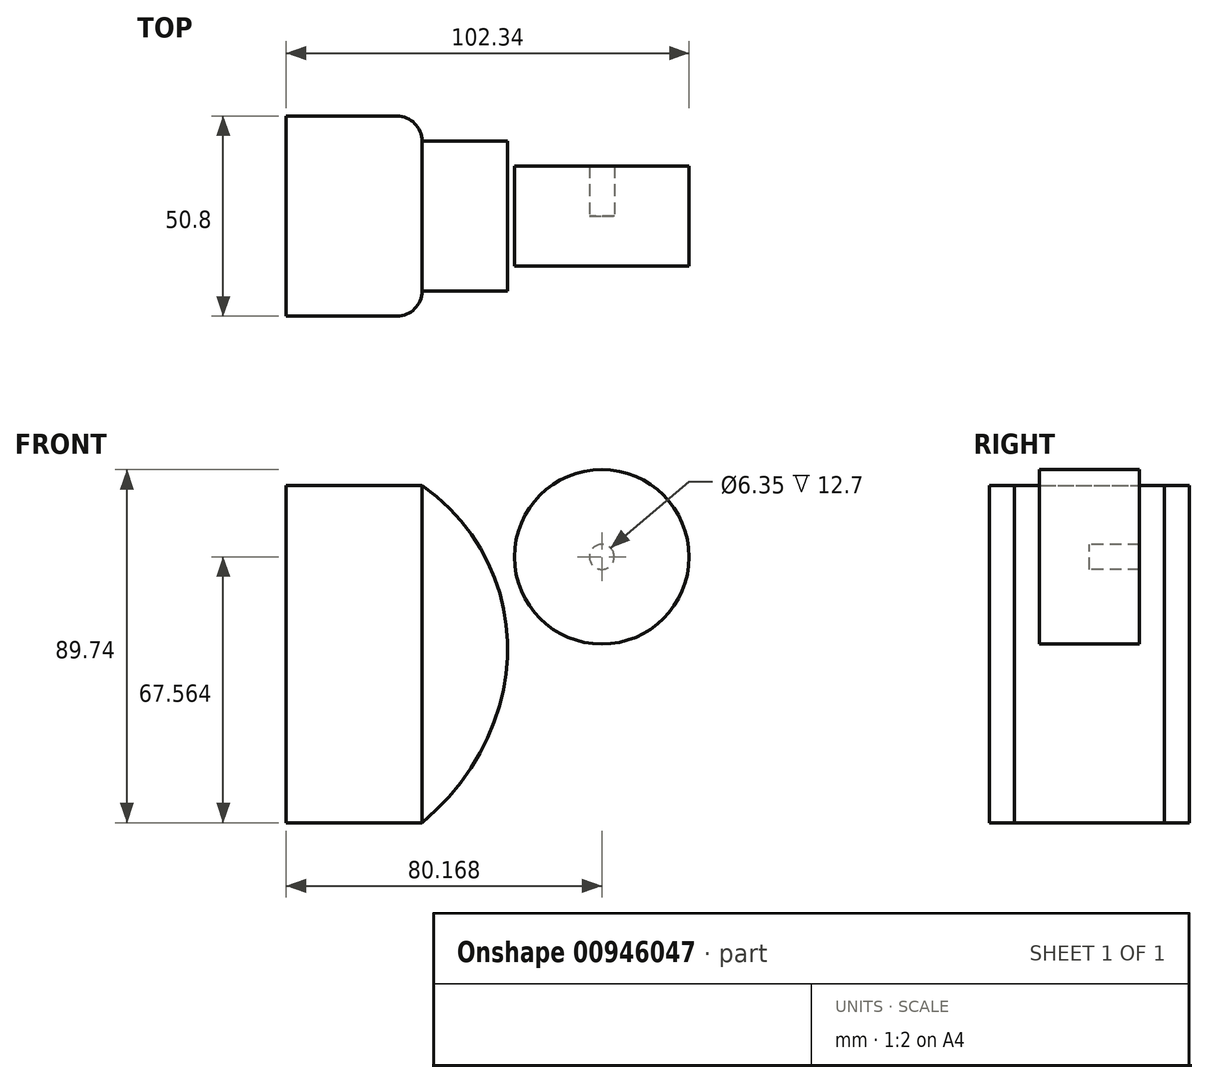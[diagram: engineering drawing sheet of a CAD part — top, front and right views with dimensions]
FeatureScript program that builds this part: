
annotation { "Feature Type Name" : "Feature", "Feature Type Description" : "" }
export const myFeature = defineFeature(function(context is Context, id is Id, definition is map)
    precondition{}
    {
        {
            var Q0;
            Q0=qCreatedBy(makeId("Front.planeOp"),FACE);
            var sketch = newSketch(context, id + "F0", { "sketchPlane" : qUnion([Q0])});
            skLineSegment(sketch, "E0.bottom", {"start": v(-47.09, -46.4) * mm, "end": v(-12.6, -46.4) * mm});
            skLineSegment(sketch, "E0.top", {"start": v(-47.09, 39.32) * mm, "end": v(-12.6, 39.32) * mm});
            skLineSegment(sketch, "E0.left", {"start": v(-47.09, -46.4) * mm, "end": v(-47.09, 39.32) * mm});
            skLineSegment(sketch, "E0.right", {"start": v(-12.6, -46.4) * mm, "end": v(-12.6, 39.32) * mm});
            skFitSpline(sketch, "E1", {"points": [v(-12.6, 39.32) * mm, v(-12.6, -46.4) * mm], "startDerivative": vector(87.62, -62.5) * mm, "endDerivative": vector(-86.21, -72.18) * mm});
            skCircle(sketch, "E2", {"center": v(33.08, 21.16) * mm, "radius": 22.18 * mm});
            skCircle(sketch, "E3.0", {"center": v(33.08, 21.16) * mm, "radius": 9.48 * mm});
            skSolve(sketch);
        }
        {
            var Q0;
            Q0=makeQuery(id+"F0.imprint","IMPRINT",FACE,{"disambiguationData":[TD([[makeQuery(id+"F0.imprint","IMPRINT",EDGE,{"derivedFrom":sQuery(id+"F0.wireOp",EDGE,"E0.bottom")}),1.0]])]});
            extrude(context, id + "F1", {"entities" : qUnion([Q0]), "endBound" : BoundingType.SYMMETRIC, "depth" : 50.8 * mm, "offsetDistance" : 25.4 * mm});
        }
        {
            var Q0;
            Q0=makeQuery(id+"F0.imprint","IMPRINT",FACE,{"disambiguationData":[TD([[makeQuery(id+"F0.imprint","IMPRINT",EDGE,{"derivedFrom":sQuery(id+"F0.wireOp",EDGE,"E0.right")}),-1.0]])]});
            extrude(context, id + "F2", {"entities" : qUnion([Q0]), "operationType" : NewBodyOperationType.ADD, "endBound" : BoundingType.SYMMETRIC, "depth" : 38.1 * mm, "offsetDistance" : 25.4 * mm});
        }
        {
            var Q0;
            Q0=makeQuery(id+"F1.opExtrude","CAP_EDGE",EDGE,{"disambiguationData":[OSD([sQuery(id+"F0.wireOp",EDGE,"E0.right")])],"isStart":false});
            var Q1;
            Q1=makeQuery(id+"F1.opExtrude","CAP_EDGE",EDGE,{"disambiguationData":[OSD([sQuery(id+"F0.wireOp",EDGE,"E0.right")])],"isStart":true});
            fillet(context, id + "F3", {"entities" : qUnion([Q0, Q1]), "radius" : 6.35 * mm, "tangentPropagation" : true, "allowEdgeOverflow" : false});
        }
        {
            var Q0;
            Q0=makeQuery(id+"F0.imprint","IMPRINT",FACE,{"disambiguationData":[TD([[makeQuery(id+"F0.imprint","IMPRINT",EDGE,{"derivedFrom":sQuery(id+"F0.wireOp",EDGE,"E2")}),1.0]])]});
            extrude(context, id + "F4", {"entities" : qUnion([Q0]), "endBound" : BoundingType.SYMMETRIC, "depth" : 25.4 * mm, "offsetDistance" : 25.4 * mm});
        }
        {
            var Q0;
            Q0=makeQuery(id+"F0.imprint","IMPRINT",FACE,{"disambiguationData":[TD([[makeQuery(id+"F0.imprint","IMPRINT",EDGE,{"derivedFrom":sQuery(id+"F0.wireOp",EDGE,"E3.0")}),1.0]])]});
            extrude(context, id + "F5", {"entities" : qUnion([Q0]), "operationType" : NewBodyOperationType.ADD, "endBound" : BoundingType.SYMMETRIC, "depth" : 25.4 * mm, "offsetDistance" : 25.4 * mm});
        }
        {
            var Q0;
            Q0=sQuery(id+"F0.wireOp",VERTEX,"E3.0.center");
            var Q1;
            Q1=makeQuery(id+"F4.opExtrude","SWEPT_BODY",BODY,{"disambiguationData":[OSD([sQuery(id+"F0.wireOp",EDGE,"E2"),sQuery(id+"F0.wireOp",EDGE,"E3.0")])]});
            var Q2;
            Q2=makeQuery(id+"F1.opExtrude","SWEPT_BODY",BODY,{"disambiguationData":[OSD([sQuery(id+"F0.wireOp",EDGE,"E0.bottom"),sQuery(id+"F0.wireOp",EDGE,"E0.top"),sQuery(id+"F0.wireOp",EDGE,"E0.left"),sQuery(id+"F0.wireOp",EDGE,"E0.right")])]});
            hole(context, id + "F6", {"style" : HoleStyle.SIMPLE, "endStyle" : HoleEndStyle.THROUGH, "holeDiameter" : 6.35 * mm, "majorDiameter" : 6.35 * mm, "isTappedThrough" : true, "tappedDepth" : 12.7 * mm, "tapClearance" : 3, "locations" : qUnion([Q0]), "scope" : qUnion([Q1, Q2])});
        }
    });
